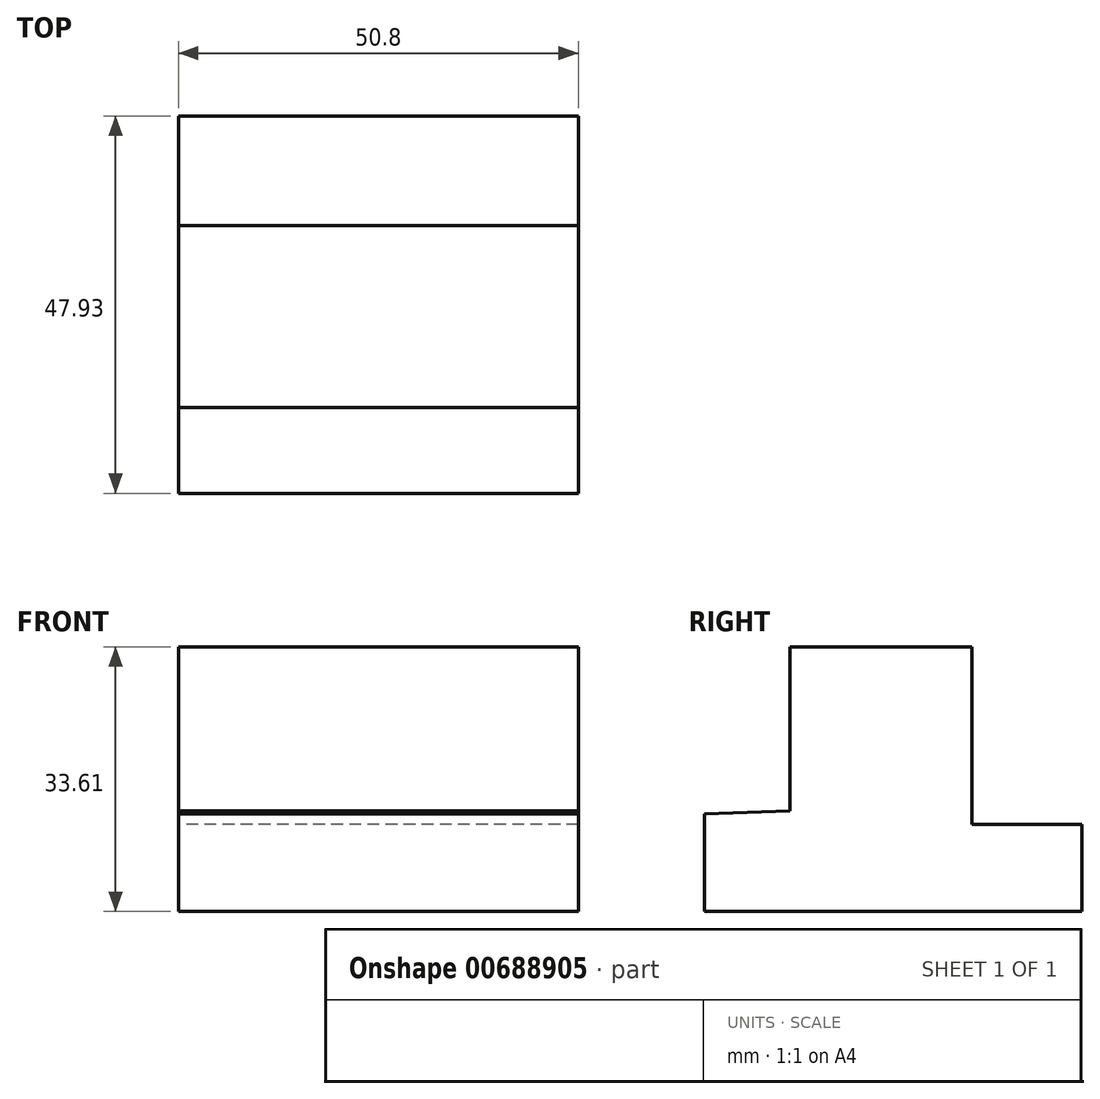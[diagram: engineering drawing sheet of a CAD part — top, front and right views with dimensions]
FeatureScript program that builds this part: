
annotation { "Feature Type Name" : "Feature", "Feature Type Description" : "" }
export const myFeature = defineFeature(function(context is Context, id is Id, definition is map)
    precondition{}
    {
        {
            var Q0;
            Q0=qCreatedBy(makeId("Right.planeOp"),FACE);
            var sketch = newSketch(context, id + "F0", { "sketchPlane" : qUnion([Q0])});
            skLineSegment(sketch, "E0", {"start": v(-52.42, -16.52) * mm, "end": v(-52.42, -28.93) * mm});
            skLineSegment(sketch, "E1", {"start": v(-52.42, -28.93) * mm, "end": v(-4.49, -28.93) * mm});
            skLineSegment(sketch, "E2", {"start": v(-4.49, -28.93) * mm, "end": v(-4.49, -17.85) * mm});
            skLineSegment(sketch, "E3", {"start": v(-4.49, -17.85) * mm, "end": v(-18.43, -17.85) * mm});
            skLineSegment(sketch, "E4", {"start": v(-18.43, -17.85) * mm, "end": v(-18.43, 4.68) * mm});
            skLineSegment(sketch, "E5", {"start": v(-18.43, 4.68) * mm, "end": v(-41.53, 4.68) * mm});
            skLineSegment(sketch, "E6", {"start": v(-41.53, 4.68) * mm, "end": v(-41.53, -16.14) * mm});
            skLineSegment(sketch, "E7", {"start": v(-41.53, -16.14) * mm, "end": v(-52.42, -16.52) * mm});
            skSolve(sketch);
        }
        {
            var Q0;
            Q0 = qSketchRegion(id + "F0", true);
            extrude(context, id + "F1", {"entities" : qUnion([Q0]), "depth" : 50.8 * mm, "offsetDistance" : 25.4 * mm});
        }
    });
